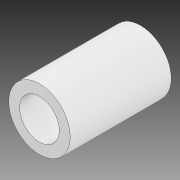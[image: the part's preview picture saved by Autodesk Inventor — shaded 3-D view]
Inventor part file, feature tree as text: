
AUTODESK INVENTOR PART (.ipt)
format: ipt  version: 2020 (Build 240168000, 168)  size: 88,064 bytes
history: native  units: mm
features: extrude x1, sketch x1
ambient origin geometry x8: Origin, YZ Plane, XZ Plane, XY Plane, X Axis, Y Axis, Z Axis, Center Point
bodies: Solid1 (feature_tree)
feature tree (2):
  extrude  "Extrusion1"  Depth=28.0mm
  sketch  "Sketch1"  dims[d0=11.0mm d1=17.0mm d2=28.0mm d3=0.0mm]
